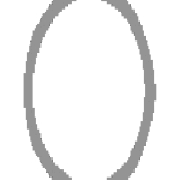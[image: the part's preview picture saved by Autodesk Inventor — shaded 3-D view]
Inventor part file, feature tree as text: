
AUTODESK INVENTOR PART (.ipt)
format: ipt  version: 2021 (Build 250183000, 183)  size: 112,640 bytes
history: native  units: in
note: dims shown in document units (in); Inventor stores cm internally (conversion verified against a paired STEP export)
features: other x4, sketch x3, plane x1
ambient origin geometry x8: Origin, YZ Plane, XZ Plane, XY Plane, X Axis, Y Axis, Z Axis, Center Point
bodies: Solid1 (feature_tree), Body (feature_tree)
feature tree (8):
  other  "Driven Length"
  other  "Frame Generator"
  other  "Start Plane"
  other  "End Plane"
  sketch  "Sketch"  dims[d2=13.5in d4=-0.0in d5=13.5in d6=0.12in d7=0.0in d8=90.0deg d9=13.5in]
  sketch  "Sketch2"  dims[d0=1.0in]
  plane  "Work Plane3"
  sketch  "Sketch3"  dims[d1=0.065in]
